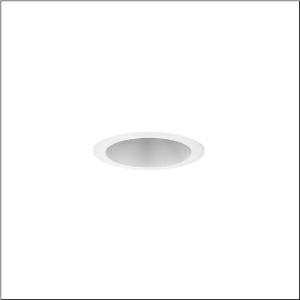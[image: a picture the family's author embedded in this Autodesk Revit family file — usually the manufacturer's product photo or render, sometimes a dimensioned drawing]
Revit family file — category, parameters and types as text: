
# Revit family: lunis_31_mini_51dn167e41
name_source: partatom
category: Lighting Fixtures
units: mm (PartAtom-declared; Revit-internal decimal feet)

## family parameters
Cut with Voids When Loaded = No
Host = Face
Light Source = No
Part Type = Normal
Room Calculation Point = No
Round Connector Dimension = Use Diameter
Shared = No

## types (1)
- Lunis 31 mini (1 x LED, 1040 lm, 8.3 W, 4000K)
    Apparent Load = 8 VA
    CIE Flux Codes = 69 93 99 100 100
    Color Rendering = 80
    Color Temperature = 4000K
    Default Elevation = 1800 mm
    Description = Lunis 31,  mini, downlight, light control with reflector, light emission: direct distribution, LED rated luminous flux: 1.040lm, light colour: 840, mains connection: 220..240V, AC, 50/60Hz, housing, white, protection rating (complete): IP20, protection rating (on room side): IP54, insulation class (complete): insulation class II (safety insulation), certification: CE, packaging unit: 1 piece
    Height = 0 mm  [stored 0 ft]
    Lamp = 1 x LED
    Lamp Light Flux = 1040 lm
    Lamp Power = 8.3 W
    Lamp count = 1
    Length = 188 mm  [stored 0.616798 ft]
    Luminous efficacy = 125 lm/W
    Manufacturer = Siteco
    ModVariant = No
    Model = 51DN167E41
    Mounting Place = Ceiling
    Mounting Type = Recessed
    Number of Poles = 1
    OnlyDefault = Yes
    Power Factor = 1
    Product Name = Lunis 31 mini
    Product group = downlight
    ProductGroupID = 400
    Protection Class = Protection class II
    Protection Degree = IP 20
    RLX_Detail_Level = 1
    RLX_Emergency_Light_Flux = 0 lm
    RLX_Emergency_Type = 0
    RLX_Emergency_Type_DB = No
    RlxData = <blob elided: 21745 chars, md5=08a040a5>
    Socket = socket
    Standby Power = 0 W
    System Light Flux = 1040 lm
    System Power = 8 W
    Type Comments = Product without accessories
    Type Image = l_1005624.jpg
    URL = http://relux.com
    VarID = ---
    Voltage = 0 V
    Weight = 0.00 kg
    Width = 0 mm  [stored 0 ft]

note: [stored X ft] marks values corroborated as IEEE doubles in the binary element streams (Revit-internal decimal feet)

## geometry (parser evidence)
native form markers: Blend x4, Sweep x11
no freeform markers — native parametric forms only
